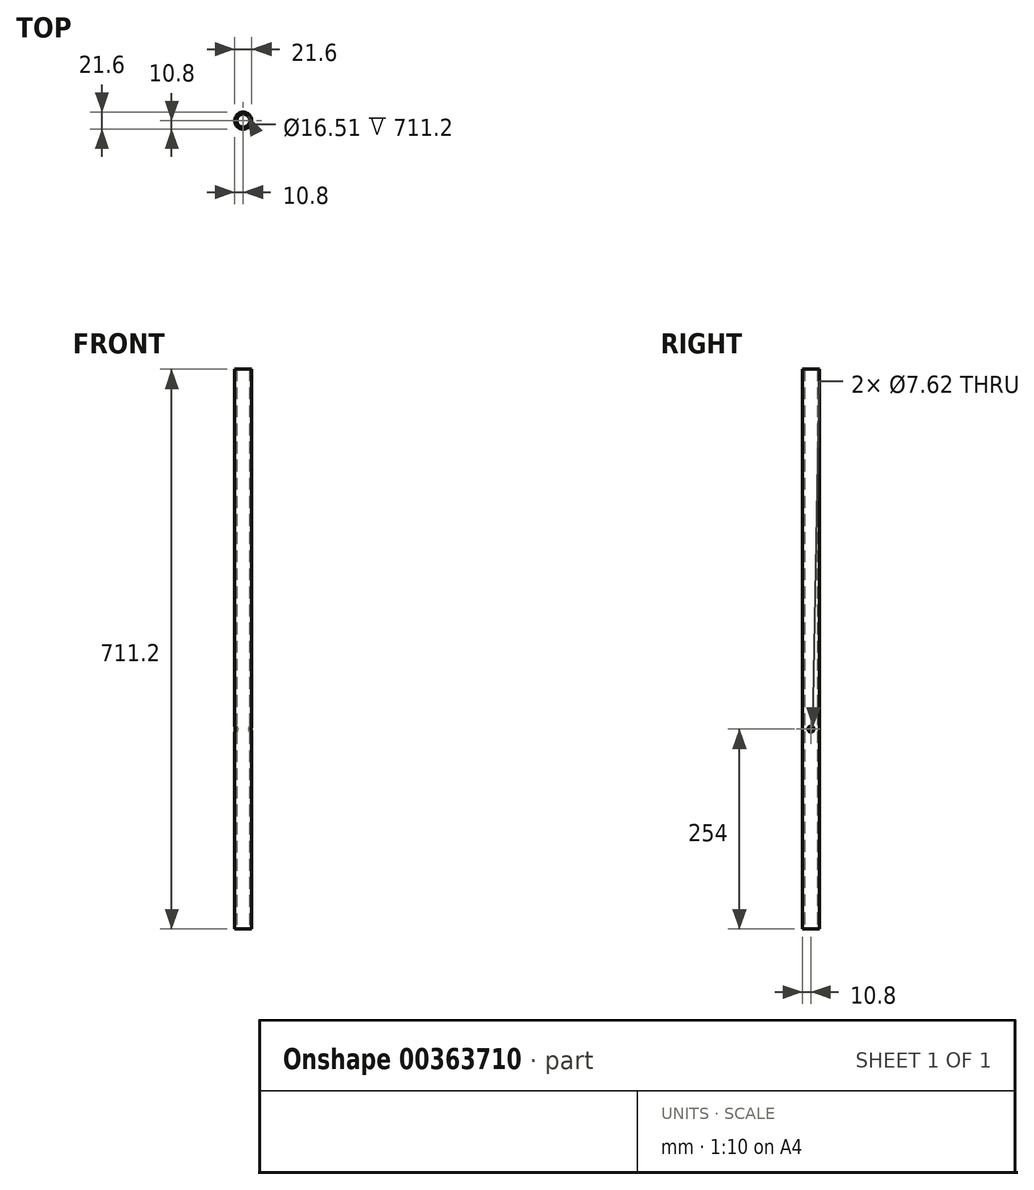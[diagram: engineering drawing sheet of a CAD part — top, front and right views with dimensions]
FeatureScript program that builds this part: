
annotation { "Feature Type Name" : "Feature", "Feature Type Description" : "" }
export const myFeature = defineFeature(function(context is Context, id is Id, definition is map)
    precondition{}
    {
        {
            var Q0;
            Q0=qCreatedBy(makeId("Top.planeOp"),FACE);
            var sketch = newSketch(context, id + "F0", { "sketchPlane" : qUnion([Q0])});
            skCircle(sketch, "E0", {"center": v(0, 0) * mm, "radius": 8.26 * mm});
            skCircle(sketch, "E1.0", {"center": v(0, 0) * mm, "radius": 10.8 * mm});
            skSolve(sketch);
        }
        {
            var Q0;
            Q0=makeQuery(id+"F0.imprint","IMPRINT",FACE,{"disambiguationData":[TD([[makeQuery(id+"F0.imprint","IMPRINT",EDGE,{"derivedFrom":sQuery(id+"F0.wireOp",EDGE,"E0")}),-1.0]])]});
            extrude(context, id + "F1", {"entities" : qUnion([Q0]), "depth" : 711.2 * mm});
        }
        {
            var Q0;
            Q0=qCreatedBy(makeId("Right.planeOp"),FACE);
            var sketch = newSketch(context, id + "F2", { "sketchPlane" : qUnion([Q0])});
            skCircle(sketch, "E2", {"center": v(0, 254) * mm, "radius": 3.81 * mm});
            skSolve(sketch);
        }
        {
            var Q0;
            Q0 = qSketchRegion(id + "F2", true);
            extrude(context, id + "F3", {"entities" : qUnion([Q0]), "operationType" : NewBodyOperationType.REMOVE, "endBound" : BoundingType.SYMMETRIC, "oppositeDirection" : true, "depth" : 25.4 * mm});
        }
    });
